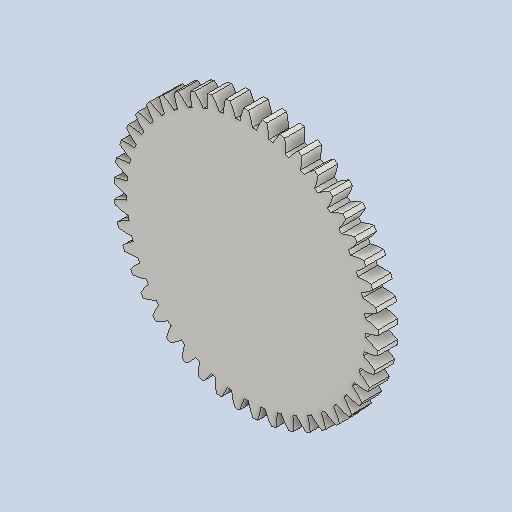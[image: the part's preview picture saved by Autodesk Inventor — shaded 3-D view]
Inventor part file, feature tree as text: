
AUTODESK INVENTOR PART (.ipt)
format: ipt  version: 2025.2 (Build 292293000, 293)  size: 316,416 bytes
history: native  units: mm (DEFAULTED — no unit token found)
features: plane x3, other x3, extrude x1, sketch x1
ambient origin geometry x8: Origin, YZ Plane, XZ Plane, XY Plane, X Axis, Y Axis, Z Axis, Center Point
bodies: Solid1 (feature_tree)
feature tree (8):
  extrude  "Extrusion1"  Depth=7.0mm TaperAngle=0.0deg
  plane  "Work Plane2"
  plane  "Work Plane8"
  plane  "Work Plane9"
  other  "Spur Gear"
  sketch  "Sketch1"  dims[d0=94.0mm d1=7.0mm d2=0.0mm d3=90.0mm d4=10.0mm d5=0.0mm d16=60.0mm d17=0.0mm d34=0.698132mm d39=0.0mm d41=0.0mm d43=60.0mm d46=60.0mm d47=0.0mm d48=0.0mm]
  other  "Srf1"
  other  "Pitch Diameter"
